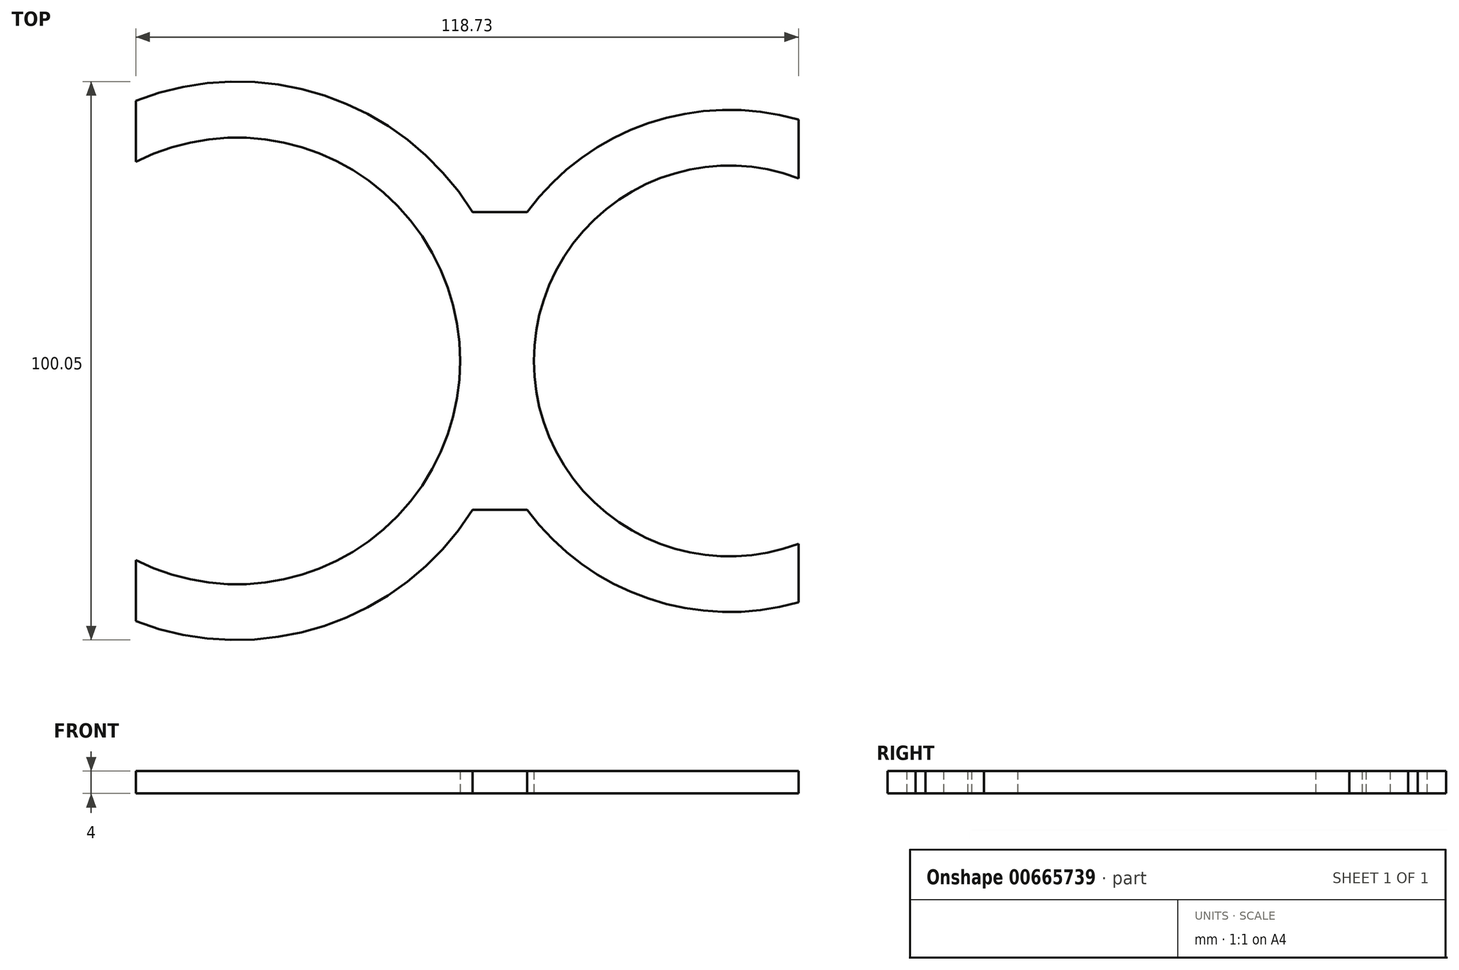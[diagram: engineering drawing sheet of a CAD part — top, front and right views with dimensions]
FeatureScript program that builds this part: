
annotation { "Feature Type Name" : "Feature", "Feature Type Description" : "" }
export const myFeature = defineFeature(function(context is Context, id is Id, definition is map)
    precondition{}
    {
        {
            var Q0;
            Q0=qCreatedBy(makeId("Top.planeOp"),FACE);
            var sketch = newSketch(context, id + "F0", { "sketchPlane" : qUnion([Q0])});
            skLineSegment(sketch, "E0", {"start": v(-86.56, 38.33) * mm, "end": v(-86.56, -38.33) * mm, "construction": true});
            skCircle(sketch, "E1", {"center": v(70.66, 0) * mm, "radius": 35 * mm, "construction": true});
            skLineSegment(sketch, "E2", {"start": v(83.05, 32.73) * mm, "end": v(83.05, -32.73) * mm, "construction": true});
            skCircle(sketch, "E3", {"center": v(70.66, 0) * mm, "radius": 45 * mm, "construction": true});
            skLineSegment(sketch, "E4", {"start": v(83.05, 32.73) * mm, "end": v(83.05, 43.26) * mm, "construction": true});
            skCircle(sketch, "E5", {"center": v(-17.6, 0) * mm, "radius": 40 * mm, "construction": true});
            skCircle(sketch, "E6", {"center": v(-17.6, 0) * mm, "radius": 50 * mm, "construction": true});
            skLineSegment(sketch, "E7", {"start": v(83.05, -32.73) * mm, "end": v(83.05, -43.26) * mm, "construction": true});
            skLineSegment(sketch, "E8", {"start": v(-35.68, 46.62) * mm, "end": v(-35.68, -46.62) * mm, "construction": true});
            skArc(sketch, "E9", {"start": v(-35.68, -46.62) * mm, "mid": v(-1.93, -47.47) * mm, "end": v(24.68, -26.69) * mm});
            skArc(sketch, "E10", {"start": v(34.43, -26.69) * mm, "mid": v(56.15, -42.56) * mm, "end": v(83.05, -43.26) * mm});
            skLineSegment(sketch, "E11", {"start": v(24.68, -26.69) * mm, "end": v(24.68, 49.26) * mm, "construction": true});
            skLineSegment(sketch, "E12", {"start": v(24.68, 49.26) * mm, "end": v(34.43, 46.82) * mm, "construction": true});
            skLineSegment(sketch, "E13", {"start": v(34.43, 46.82) * mm, "end": v(34.43, -26.69) * mm, "construction": true});
            skArc(sketch, "E14", {"start": v(24.68, 26.69) * mm, "mid": v(-1.9, 47.56) * mm, "end": v(-35.68, 46.62) * mm});
            skArc(sketch, "E15", {"start": v(83.05, 43.26) * mm, "mid": v(56.15, 42.58) * mm, "end": v(34.43, 26.69) * mm});
            skLineSegment(sketch, "E16", {"start": v(24.68, -26.69) * mm, "end": v(34.43, -26.69) * mm});
            skLineSegment(sketch, "E17", {"start": v(24.68, 26.69) * mm, "end": v(34.43, 26.69) * mm});
            skLineSegment(sketch, "E18", {"start": v(83.05, -43.26) * mm, "end": v(83.05, -32.73) * mm});
            skLineSegment(sketch, "E19", {"start": v(83.05, 32.73) * mm, "end": v(83.05, 43.26) * mm});
            skLineSegment(sketch, "E20", {"start": v(-35.68, -46.62) * mm, "end": v(-35.68, -35.68) * mm});
            skLineSegment(sketch, "E21", {"start": v(-35.68, 46.62) * mm, "end": v(-35.68, 35.68) * mm});
            skArc(sketch, "E22", {"start": v(-35.68, -35.68) * mm, "mid": v(22.44, 0) * mm, "end": v(-35.68, 35.68) * mm});
            skArc(sketch, "E23", {"start": v(83.05, 32.73) * mm, "mid": v(35.64, 0) * mm, "end": v(83.05, -32.73) * mm});
            skSolve(sketch);
        }
        {
            var Q0;
            Q0=makeQuery(id+"F0.imprint","IMPRINT",FACE,{"disambiguationData":[TD([[makeQuery(id+"F0.imprint","IMPRINT",EDGE,{"derivedFrom":sQuery(id+"F0.wireOp",EDGE,"E9")}),1.0]])]});
            extrude(context, id + "F1", {"entities" : qUnion([Q0]), "depth" : 4 * mm, "offsetDistance" : 25 * mm});
        }
    });
